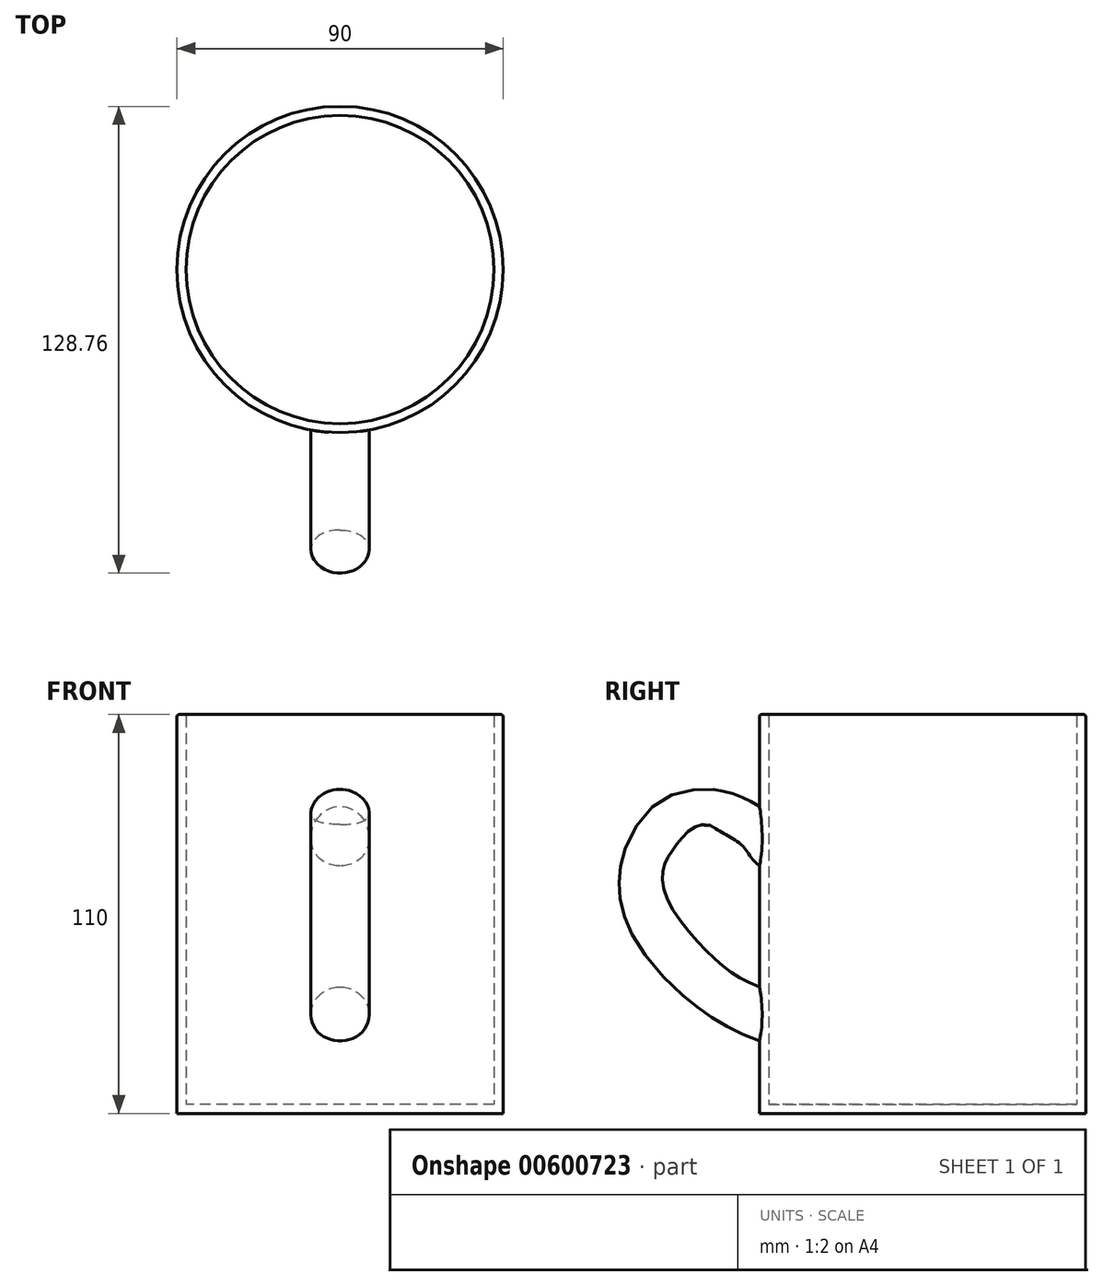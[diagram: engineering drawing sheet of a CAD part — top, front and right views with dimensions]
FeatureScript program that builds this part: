
annotation { "Feature Type Name" : "Feature", "Feature Type Description" : "" }
export const myFeature = defineFeature(function(context is Context, id is Id, definition is map)
    precondition{}
    {
        {
            var Q0;
            Q0=qCreatedBy(makeId("Top.planeOp"),FACE);
            var sketch = newSketch(context, id + "F0", { "sketchPlane" : qUnion([Q0])});
            skCircle(sketch, "E0", {"center": v(0, -1.83) * mm, "radius": 45 * mm});
            skSolve(sketch);
        }
        {
            var Q0;
            Q0=makeQuery(id+"F0.imprint","IMPRINT",FACE,{"disambiguationData":[TD([[makeQuery(id+"F0.imprint","IMPRINT",EDGE,{"derivedFrom":sQuery(id+"F0.wireOp",EDGE,"E0")}),1.0]])]});
            extrude(context, id + "F1", {"entities" : qUnion([Q0]), "depth" : 110 * mm, "offsetDistance" : 25 * mm});
        }
        {
            var Q0;
            Q0=qCreatedBy(makeId("Right.planeOp"),FACE);
            var sketch = newSketch(context, id + "F2", { "sketchPlane" : qUnion([Q0])});
            skFitSpline(sketch, "E1", {"points": [v(-42.3, 83.64) * mm, v(-56.11, 90.34) * mm, v(-75.9, 86.93) * mm, v(-86.94, 66.55) * mm, v(-81.5, 45.38) * mm, v(-60.29, 24.83) * mm, v(-42.57, 16.77) * mm], "startDerivative": vector(-89.08, 58.52) * mm, "endDerivative": vector(108.27, -38.68) * mm});
            skSolve(sketch);
        }
        {
            var Q0;
            Q0=qCreatedBy(makeId("Front.planeOp"),FACE);
            cPlane(context, id + "F3", {"entities" : qUnion([Q0]), "cplaneType" : CPlaneType.OFFSET, "offset" : 48 * mm, "width" : 150 * mm, "height" : 150 * mm});
        }
        {
            var Q0;
            Q0=qCreatedBy(id+"F3.planeOp",FACE);
            var sketch = newSketch(context, id + "F4", { "sketchPlane" : qUnion([Q0])});
            skCircle(sketch, "E2", {"center": v(0, 77.36) * mm, "radius": 8.02 * mm});
            skSolve(sketch);
        }
        {
            var Q0;
            Q0=makeQuery(id+"F4.imprint","IMPRINT",FACE,{"disambiguationData":[TD([[makeQuery(id+"F4.imprint","IMPRINT",EDGE,{"derivedFrom":sQuery(id+"F4.wireOp",EDGE,"E2")}),1.0]])]});
            var Q1;
            Q1=sQuery(id+"F2.wireOp",EDGE,"E1");
            sweep(context, id + "F5", {"operationType" : NewBodyOperationType.ADD, "profiles" : qUnion([Q0]), "path" : qUnion([Q1])});
        }
        {
            var Q0;
            Q0=makeQuery(id+"F1.opExtrude","CAP_FACE",FACE,{"disambiguationData":[OSD([sQuery(id+"F0.wireOp",EDGE,"E0")])],"isStart":false});
            shell(context, id + "F6", {"entities" : qUnion([Q0]), "thickness" : 2.5 * mm});
        }
        {
            var Q0;
            {var subQ0=sQuery(id+"F0.wireOp",EDGE,"E0");Q0=makeQuery(id+"F6.opShell","OFFSET_EDGE",EDGE,{"disambiguationData":[OSD([subQ0]),TDD([makeQuery(id+"F1.opExtrude","CAP_EDGE",EDGE,{"disambiguationData":[OSD([subQ0])],"isStart":false})])]});}
            var Q1;
            Q1=makeQuery(id+"F1.opExtrude","CAP_EDGE",EDGE,{"disambiguationData":[OSD([sQuery(id+"F0.wireOp",EDGE,"E0")])],"isStart":false});
            fillet(context, id + "F7", {"entities" : qUnion([Q0, Q1]), "radius" : 0.5 * mm, "tangentPropagation" : true, "allowEdgeOverflow" : false});
        }
    });
